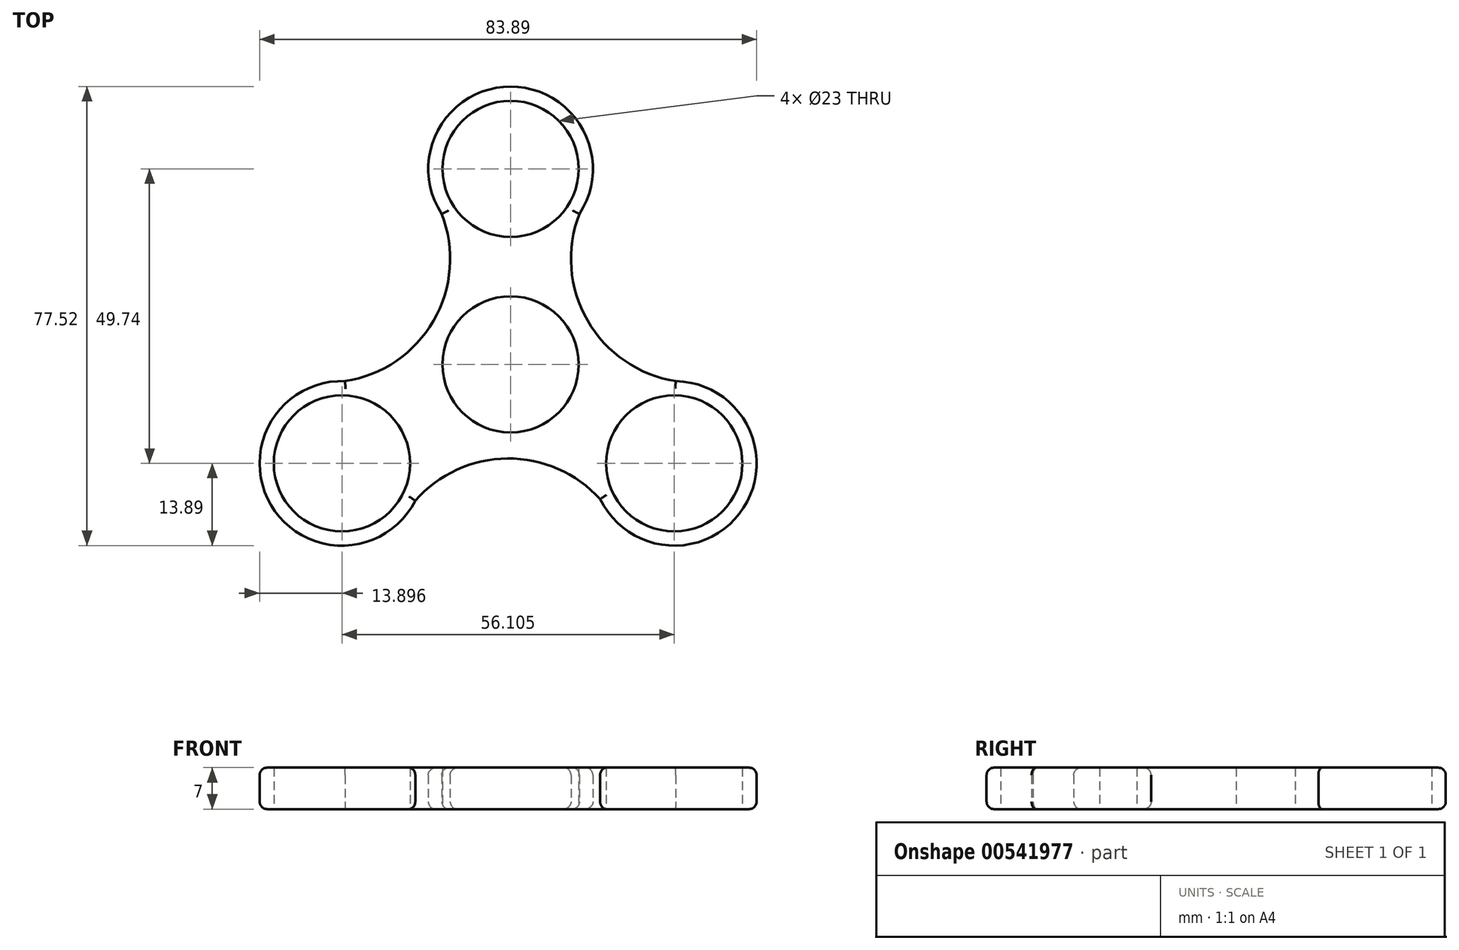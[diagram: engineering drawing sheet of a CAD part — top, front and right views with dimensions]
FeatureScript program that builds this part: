
annotation { "Feature Type Name" : "Feature", "Feature Type Description" : "" }
export const myFeature = defineFeature(function(context is Context, id is Id, definition is map)
    precondition{}
    {
        {
            var Q0;
            Q0=qCreatedBy(makeId("Top.planeOp"),FACE);
            var sketch = newSketch(context, id + "F0", { "sketchPlane" : qUnion([Q0])});
            skCircle(sketch, "E0", {"center": v(0, 0) * mm, "radius": 11.5 * mm});
            skLineSegment(sketch, "E1", {"start": v(0, 0) * mm, "end": v(0, 33.02) * mm, "construction": true});
            skLineSegment(sketch, "E2", {"start": v(0, 0) * mm, "end": v(27.77, -17.86) * mm, "construction": true});
            skCircle(sketch, "E3", {"center": v(-28.47, -16.72) * mm, "radius": 11.5 * mm});
            skCircle(sketch, "E4", {"center": v(0, 33.02) * mm, "radius": 11.5 * mm});
            skLineSegment(sketch, "E5", {"start": v(0, 0) * mm, "end": v(-28.47, -16.72) * mm, "construction": true});
            skCircle(sketch, "E6", {"center": v(-28.47, -16.72) * mm, "radius": 13.9 * mm});
            skCircle(sketch, "E7", {"center": v(0, 33.02) * mm, "radius": 13.9 * mm});
            skArc(sketch, "E8", {"start": v(-27.94, -2.84) * mm, "mid": v(-13, 7.37) * mm, "end": v(-11.62, 25.4) * mm});
            skArc(sketch, "E9.MirrorCS", {"start": v(27.94, -2.84) * mm, "mid": v(13, 7.37) * mm, "end": v(11.62, 25.4) * mm});
            skLineSegment(sketch, "E10", {"start": v(-27.94, -2.84) * mm, "end": v(-27.94, -41.12) * mm, "construction": true});
            skCircle(sketch, "E11", {"center": v(27.63, -16.72) * mm, "radius": 11.5 * mm});
            skCircle(sketch, "E12", {"center": v(27.63, -16.72) * mm, "radius": 13.9 * mm});
            skLineSegment(sketch, "E13", {"start": v(27.94, -2.84) * mm, "end": v(27.94, -36.2) * mm, "construction": true});
            skLineSegment(sketch, "E14", {"start": v(27.94, -2.84) * mm, "end": v(7.74, -34.23) * mm, "construction": true});
            skLineSegment(sketch, "E15", {"start": v(-27.94, -2.84) * mm, "end": v(-8.6, -35.77) * mm, "construction": true});
            skArc(sketch, "E16", {"start": v(15.12, -22.77) * mm, "mid": v(-0.54, -15.9) * mm, "end": v(-16.09, -23.02) * mm});
            skSolve(sketch);
        }
        {
            var Q0;
            Q0 = qSketchRegion(id + "F0", true);
            extrude(context, id + "F1", {"entities" : qUnion([Q0]), "depth" : 7 * mm, "offsetDistance" : 25.4 * mm});
        }
        {
            var Q0;
            Q0=makeQuery(id+"F1.opExtrude","CAP_EDGE",EDGE,{"disambiguationData":[OSD([sQuery(id+"F0.wireOp",EDGE,"E8")])],"isStart":false});
            var Q1;
            Q1=makeQuery(id+"F1.opExtrude","CAP_EDGE",EDGE,{"disambiguationData":[OSD([sQuery(id+"F0.wireOp",EDGE,"E16")])],"isStart":false});
            var Q2;
            Q2=makeQuery(id+"F1.opExtrude","CAP_EDGE",EDGE,{"disambiguationData":[OSD([sQuery(id+"F0.wireOp",EDGE,"E9.MirrorCS")])],"isStart":false});
            var Q3;
            Q3=makeQuery(id+"F1.opExtrude","CAP_EDGE",EDGE,{"disambiguationData":[OSD([sQuery(id+"F0.wireOp",EDGE,"E16")])],"isStart":true});
            var Q4;
            Q4=makeQuery(id+"F1.opExtrude","CAP_EDGE",EDGE,{"disambiguationData":[OSD([sQuery(id+"F0.wireOp",EDGE,"E8")])],"isStart":true});
            var Q5;
            Q5=makeQuery(id+"F1.opExtrude","CAP_EDGE",EDGE,{"disambiguationData":[OSD([sQuery(id+"F0.wireOp",EDGE,"E9.MirrorCS")])],"isStart":true});
            var Q6;
            Q6=makeQuery(id+"F1.opExtrude","CAP_EDGE",EDGE,{"disambiguationData":[OSD([sQuery(id+"F0.wireOp",EDGE,"E6")])],"isStart":true});
            var Q7;
            Q7=makeQuery(id+"F1.opExtrude","CAP_EDGE",EDGE,{"disambiguationData":[OSD([sQuery(id+"F0.wireOp",EDGE,"E12")])],"isStart":true});
            var Q8;
            Q8=makeQuery(id+"F1.opExtrude","CAP_EDGE",EDGE,{"disambiguationData":[OSD([sQuery(id+"F0.wireOp",EDGE,"E7")])],"isStart":true});
            var Q9;
            Q9=makeQuery(id+"F1.opExtrude","CAP_EDGE",EDGE,{"disambiguationData":[OSD([sQuery(id+"F0.wireOp",EDGE,"E7")])],"isStart":false});
            var Q10;
            Q10=makeQuery(id+"F1.opExtrude","CAP_EDGE",EDGE,{"disambiguationData":[OSD([sQuery(id+"F0.wireOp",EDGE,"E12")])],"isStart":false});
            var Q11;
            Q11=makeQuery(id+"F1.opExtrude","CAP_EDGE",EDGE,{"disambiguationData":[OSD([sQuery(id+"F0.wireOp",EDGE,"E6")])],"isStart":false});
            fillet(context, id + "F2", {"entities" : qUnion([Q0, Q1, Q2, Q3, Q4, Q5, Q6, Q7, Q8, Q9, Q10, Q11]), "radius" : 1.27 * mm, "tangentPropagation" : true, "allowEdgeOverflow" : false});
        }
    });
